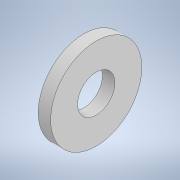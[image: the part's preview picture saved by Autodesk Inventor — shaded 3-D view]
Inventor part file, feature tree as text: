
AUTODESK INVENTOR PART (.ipt)
format: ipt  version: 2021 (Build 250183000, 183)  size: 97,792 bytes
history: native  units: mm
features: extrude x1, sketch x1
ambient origin geometry x8: Origin, YZ Plane, XZ Plane, XY Plane, X Axis, Y Axis, Z Axis, Center Point
bodies: Solid1 (feature_tree)
feature tree (2):
  extrude  "Extrusion1"  Depth=3.0mm
  sketch  "Sketch1"  dims[d0=9.0mm d1=22.0mm d2=3.0mm d3=0.0mm]
